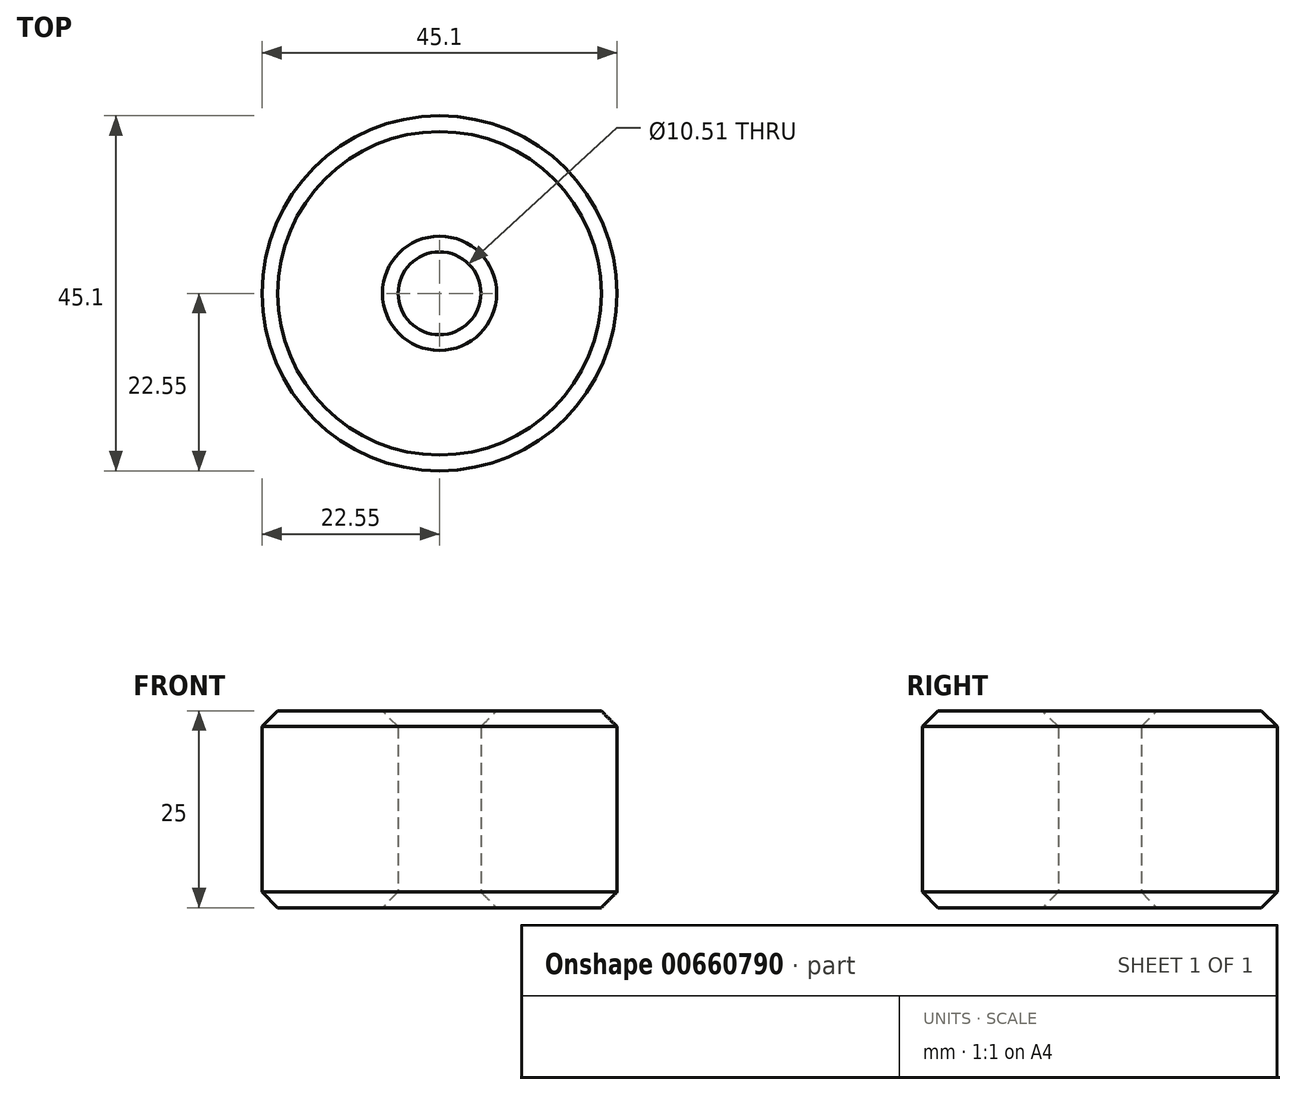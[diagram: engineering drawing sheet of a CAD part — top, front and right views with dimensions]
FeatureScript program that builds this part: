
annotation { "Feature Type Name" : "Feature", "Feature Type Description" : "" }
export const myFeature = defineFeature(function(context is Context, id is Id, definition is map)
    precondition{}
    {
        {
            var Q0;
            Q0=qCreatedBy(makeId("Top.planeOp"),FACE);
            var sketch = newSketch(context, id + "F0", { "sketchPlane" : qUnion([Q0])});
            skCircle(sketch, "E0", {"center": v(0, 0) * mm, "radius": 5.25 * mm});
            skCircle(sketch, "E1", {"center": v(0, 0) * mm, "radius": 22.55 * mm});
            skSolve(sketch);
        }
        {
            var Q0;
            Q0=makeQuery(id+"F0.imprint","IMPRINT",FACE,{"disambiguationData":[TD([[makeQuery(id+"F0.imprint","IMPRINT",EDGE,{"derivedFrom":sQuery(id+"F0.wireOp",EDGE,"E0")}),-1.0]])]});
            extrude(context, id + "F1", {"entities" : qUnion([Q0]), "depth" : 25 * mm, "offsetDistance" : 25 * mm});
        }
        {
            var Q0;
            Q0=makeQuery(id+"F1.opExtrude","CAP_EDGE",EDGE,{"disambiguationData":[OSD([sQuery(id+"F0.wireOp",EDGE,"E1")])],"isStart":false});
            var Q1;
            Q1=makeQuery(id+"F1.opExtrude","CAP_EDGE",EDGE,{"disambiguationData":[OSD([sQuery(id+"F0.wireOp",EDGE,"E1")])],"isStart":true});
            var Q2;
            Q2=makeQuery(id+"F1.opExtrude","CAP_EDGE",EDGE,{"disambiguationData":[OSD([sQuery(id+"F0.wireOp",EDGE,"E0")])],"isStart":false});
            var Q3;
            Q3=makeQuery(id+"F1.opExtrude","CAP_EDGE",EDGE,{"disambiguationData":[OSD([sQuery(id+"F0.wireOp",EDGE,"E0")])],"isStart":true});
            chamfer(context, id + "F2", {"entities" : qUnion([Q0, Q1, Q2, Q3]), "width" : 2 * mm, "tangentPropagation" : true});
        }
    });
